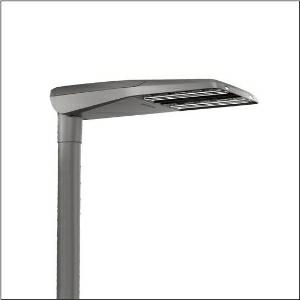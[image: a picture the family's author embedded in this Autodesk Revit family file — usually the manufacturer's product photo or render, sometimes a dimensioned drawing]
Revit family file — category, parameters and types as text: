
# Revit family: streetlight_sl_11_iq_midi___st0_5a_5xc3b51f08le_567a
name_source: partatom
category: Lighting Fixtures
units: mm (PartAtom-declared; Revit-internal decimal feet)

## family parameters
Cut with Voids When Loaded = No
Host = Face
Light Source = No
Part Type = Normal
Room Calculation Point = No
Round Connector Dimension = Use Diameter
Shared = No

## types (1)
- --- (1 x LED, 9120 lm, 60.4 W, 3000K)
    Apparent Load = 60 VA
    CIE Flux Codes = 43 74 97 100 100
    Color Rendering = 70
    Color Temperature = 3000K
    Default Elevation = 1800 mm
    Description = Streetlight SL 11 iQ midi, mast luminaire, primary light control with 3 zone facetted reflector, of plastic, silver coated, highly specular, primary optical cover: cover, of PMMA, transparent, light distribution: ST0.5a, light emission: direct distribution, primary light characteristic: asymmetric, installation type: post-top, side-entry, LED, High Power LED, rated luminous flux: 9.120lm, luminous efficacy: 151lm/W, light colour: 730, colour temperature: 3000K, control: Street-Remote, optimised constant luminous flux control (CLO 2.0), Desk-Remote (wireless, voltage-free reading and setting of iQ features in the workshop via application-optimized NFC function/RFID function), Light-Fading, Smart-Wire, Night-Set, Lumen-Switch, Temp-Guard, Auto-Match, with cable H07RN-F 5x 1.5mm², mains connection: 220..240V, AC, 50/60Hz, connection cable pre-assembled, cable length: 8,5m, start of lifetime: 60W, end of lifetime: 63W, reduction: 30W, luminaire housing, of diecast aluminium, powder-coated, Siteco® metallic grey (DB 702S), length: 780mm, width: 376mm, height: 118mm, spigot size: 60/76mm (post-top) and 42/60/76mm (side-entry), mast flange for spigot size: 42mm: 5XC10008XM4, 60mm: 5XC10008XM2, 76/60mm: 5XC10108XM1, equipment: standard, protection rating (complete): IP66, insulation class (complete): insulation class II (safety insulation), certification: CE, ENEC, VDE, impact resistance: IK09, permissible operating ambient temperature for outdoor applications: -25..+50°C, standard-compliant lighting for roads and squares, packaging unit: 1 piece

Light Distribution: ST0.5a
    Height = 118 mm
    Lamp = 1 x LED
    Lamp Light Flux = 9120 lm
    Lamp Power = 60.4 W
    Lamp count = 1
    Length = 780 mm
    Luminous efficacy = 151 lm/W
    Manufacturer = Siteco
    ModVariant = No
    Model = 5XC3B51F08LE
    Number of Poles = 1
    OnlyDefault = Yes
    Power Factor = 1
    Product Name = Streetlight SL 11 iQ midi | ST0.5a
    Product group = mast luminaire | pylon top
    ProductGroupID = 6100
    Protection Class = Protection class II
    Protection Degree = IP 66
    RLX_Detail_Level = 1
    RlxData = <blob elided: 74845 chars, md5=9f877a22>
    Socket = socket
    Standby Power = 0 W
    System Light Flux = 9120 lm
    System Power = 60 W
    Type Comments = factory setting: luminous flux: 100 % | dim-lin: 254 | 520 mA
    Type Image = l_1005960.jpg
    URL = http://relux.com
    VarID = @adj_086821
    Voltage = 0 V
    Weight = 0.00 kg
    Width = 376 mm

## geometry (parser evidence)
native form markers: Blend x4, Sweep x12
no freeform markers — native parametric forms only
